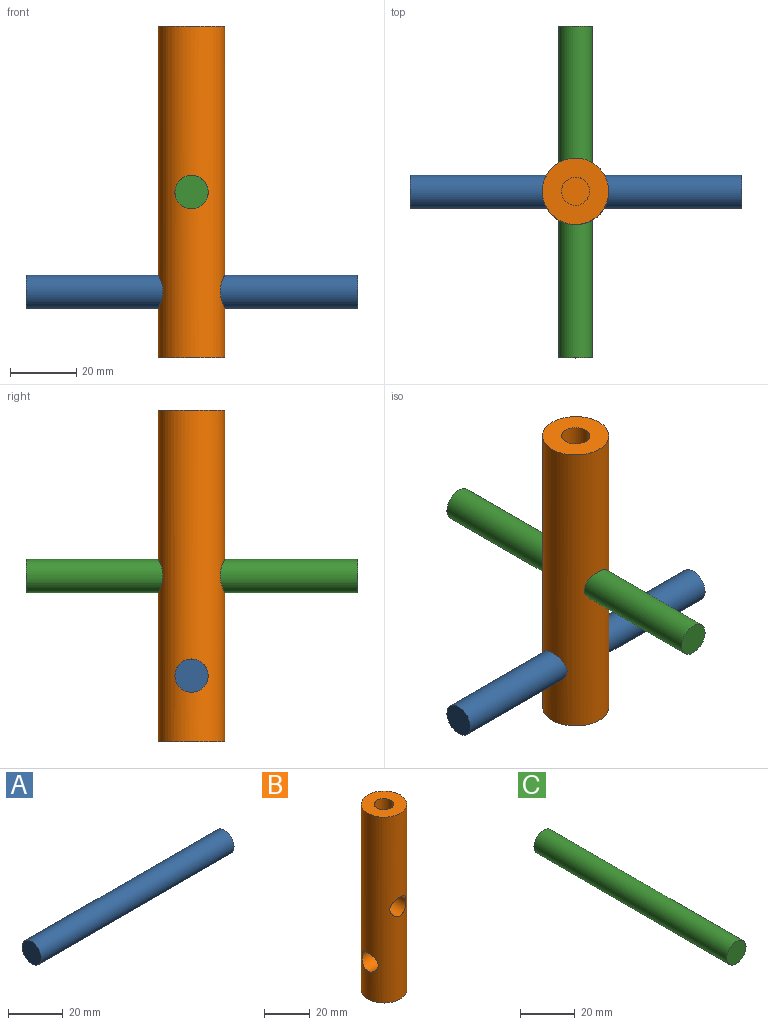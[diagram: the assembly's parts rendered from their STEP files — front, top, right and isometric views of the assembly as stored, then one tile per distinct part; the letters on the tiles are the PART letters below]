
ASSEMBLY  parts=3 mates=2
PART A: 3 faces, bbox 100x10x10 mm
  f0: cylinder r=5mm len=100mm, axis (-1,0,0), area 3141.6mm2, adj f1,f2
  f1: plane 10x10mm, normal (1,0,0), area 78.5mm2, adj f0
  f2: plane 10x10mm, normal (-1,0,0), area 78.5mm2, adj f0
PART B: 7 faces, bbox 20x20x100 mm
  f0: cylinder r=10mm len=100mm, axis (0,0,-1), area 5958mm2, adj f1,f3,f5,f6
  f1: plane 20x20mm, normal (0,0,-1), area 314.2mm2, adj f0
  f2: cylinder r=4.25mm len=25mm, axis (0,0,-1), area 667.6mm2, adj f3,f4
  f3: plane 20x20mm, normal (0,0,1), area 257.4mm2, adj f0,f2
  f4: plane 8.5x8.5mm, normal (0,0,1), area 56.7mm2, adj f2
  f5: cylinder r=5mm len=20mm, axis (1,0,0), area 587mm2, adj f0
  f6: cylinder r=5mm len=20mm, axis (0,-1,0), area 587mm2, adj f0
PART C: 3 faces, bbox 10x100x10 mm
  f0: cylinder r=5mm len=100mm, axis (0,1,0), area 3141.6mm2, adj f1,f2
  f1: plane 10x10mm, normal (0,-1,0), area 78.5mm2, adj f0
  f2: plane 10x10mm, normal (0,1,0), area 78.5mm2, adj f0
PLACE A t=(0.1,0.01,-10.64)mm
PLACE B t=(-0.04,0.01,-10.64)mm
PLACE C t=(-0.04,-0.12,-10.64)mm
MATE fastened C.f0 <-> B.f6  axis (0,-1,0) through (-0.04,-50.12,39.36)mm
MATE fastened A.f0 <-> B.f5  axis (1,0,0) through (50.1,0.01,9.36)mm
